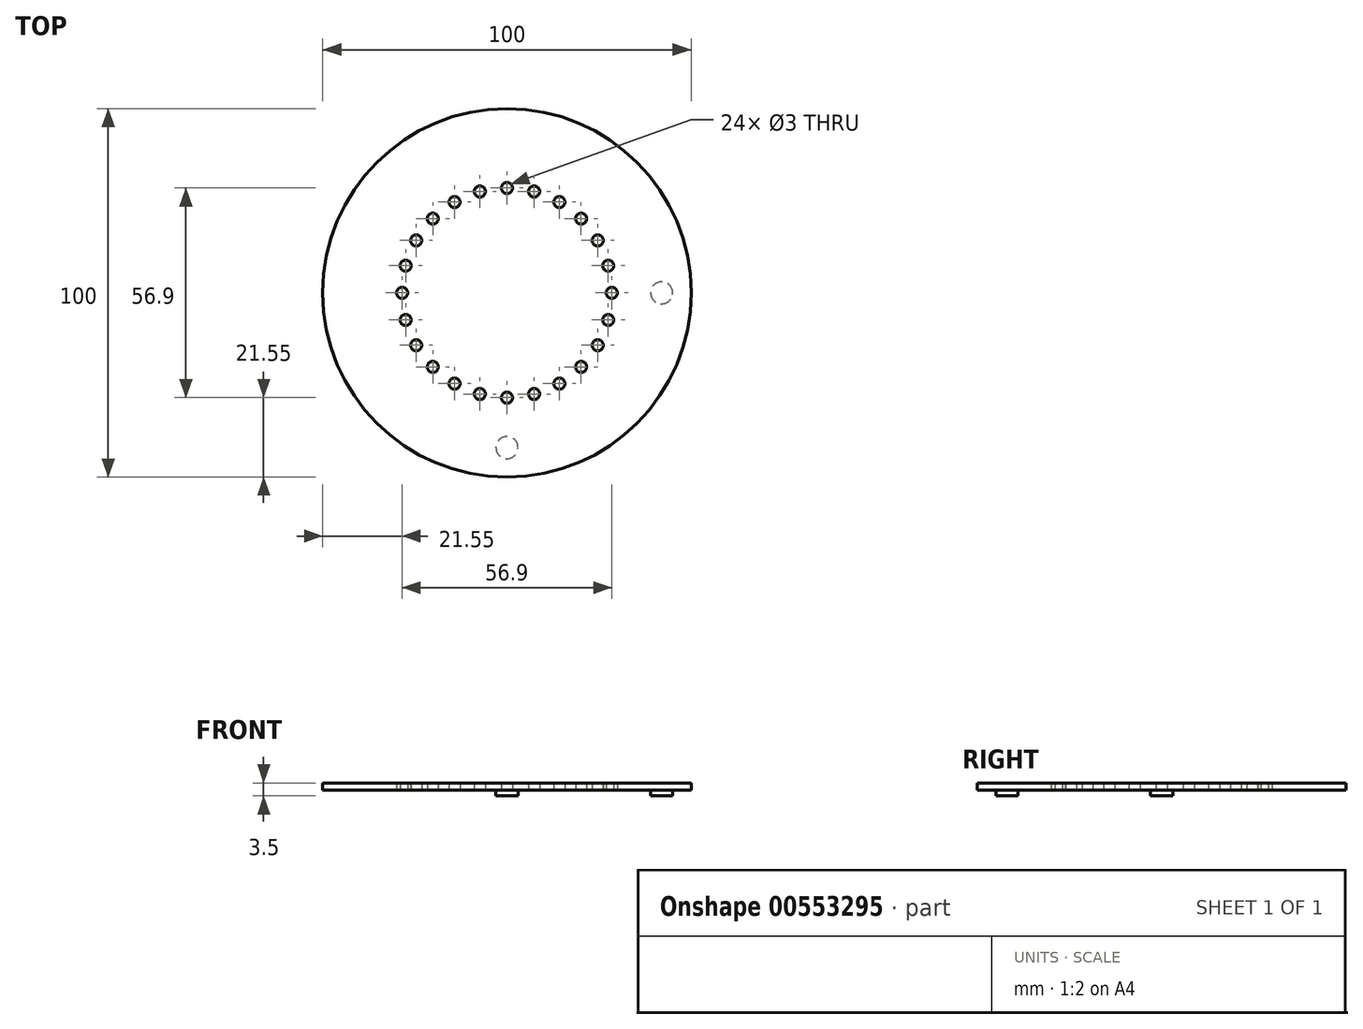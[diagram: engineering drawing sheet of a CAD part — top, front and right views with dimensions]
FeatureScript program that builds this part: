
annotation { "Feature Type Name" : "Feature", "Feature Type Description" : "" }
export const myFeature = defineFeature(function(context is Context, id is Id, definition is map)
    precondition{}
    {
        {
            var Q0;
            Q0=qCreatedBy(makeId("Top.planeOp"),FACE);
            var sketch = newSketch(context, id + "F0", { "sketchPlane" : qUnion([Q0])});
            skCircle(sketch, "E0", {"center": v(0, 0) * mm, "radius": 50 * mm});
            skCircle(sketch, "E1", {"center": v(0, 28.45) * mm, "radius": 1.5 * mm});
            skCircle(sketch, "E2.1.0", {"center": v(-7.36, 27.48) * mm, "radius": 1.5 * mm});
            skCircle(sketch, "E2.2.0", {"center": v(-14.22, 24.64) * mm, "radius": 1.5 * mm});
            skCircle(sketch, "E3.1.3.0", {"center": v(-20.12, 20.12) * mm, "radius": 1.5 * mm});
            skCircle(sketch, "E3.1.4.0", {"center": v(-24.64, 14.23) * mm, "radius": 1.5 * mm});
            skCircle(sketch, "E3.1.5.0", {"center": v(-27.48, 7.36) * mm, "radius": 1.5 * mm});
            skCircle(sketch, "E3.1.6.0", {"center": v(-28.45, 0) * mm, "radius": 1.5 * mm});
            skCircle(sketch, "E3.1.7.0", {"center": v(-27.48, -7.36) * mm, "radius": 1.5 * mm});
            skCircle(sketch, "E3.1.8.0", {"center": v(-24.64, -14.22) * mm, "radius": 1.5 * mm});
            skCircle(sketch, "E3.1.9.0", {"center": v(-20.12, -20.12) * mm, "radius": 1.5 * mm});
            skCircle(sketch, "E3.1.10.0", {"center": v(-14.22, -24.64) * mm, "radius": 1.5 * mm});
            skCircle(sketch, "E3.1.11.0", {"center": v(-7.36, -27.48) * mm, "radius": 1.5 * mm});
            skCircle(sketch, "E3.1.12.0", {"center": v(0, -28.45) * mm, "radius": 1.5 * mm});
            skCircle(sketch, "E3.1.13.0", {"center": v(7.36, -27.48) * mm, "radius": 1.5 * mm});
            skCircle(sketch, "E3.1.14.0", {"center": v(14.22, -24.64) * mm, "radius": 1.5 * mm});
            skCircle(sketch, "E3.1.15.0", {"center": v(20.12, -20.12) * mm, "radius": 1.5 * mm});
            skCircle(sketch, "E3.1.16.0", {"center": v(24.64, -14.23) * mm, "radius": 1.5 * mm});
            skCircle(sketch, "E3.1.17.0", {"center": v(27.48, -7.36) * mm, "radius": 1.5 * mm});
            skCircle(sketch, "E3.1.18.0", {"center": v(28.45, 0) * mm, "radius": 1.5 * mm});
            skCircle(sketch, "E3.1.19.0", {"center": v(27.48, 7.36) * mm, "radius": 1.5 * mm});
            skCircle(sketch, "E3.1.20.0", {"center": v(24.64, 14.23) * mm, "radius": 1.5 * mm});
            skCircle(sketch, "E3.1.21.0", {"center": v(20.12, 20.12) * mm, "radius": 1.5 * mm});
            skCircle(sketch, "E3.1.22.0", {"center": v(14.23, 24.64) * mm, "radius": 1.5 * mm});
            skCircle(sketch, "E3.1.23.0", {"center": v(7.36, 27.48) * mm, "radius": 1.5 * mm});
            skSolve(sketch);
        }
        {
            var Q0;
            Q0=makeQuery(id+"F0.imprint","IMPRINT",FACE,{"disambiguationData":[TD([[makeQuery(id+"F0.imprint","IMPRINT",EDGE,{"derivedFrom":sQuery(id+"F0.wireOp",EDGE,"E0")}),1.0]])]});
            extrude(context, id + "F1", {"entities" : qUnion([Q0]), "depth" : 2 * mm, "offsetDistance" : 25 * mm});
        }
        {
            var Q0;
            Q0=makeQuery(id+"F1.opExtrude","CAP_FACE",FACE,{"disambiguationData":[OSD([sQuery(id+"F0.wireOp",EDGE,"E0"),sQuery(id+"F0.wireOp",EDGE,"E1"),sQuery(id+"F0.wireOp",EDGE,"E2.1.0"),sQuery(id+"F0.wireOp",EDGE,"E2.2.0"),sQuery(id+"F0.wireOp",EDGE,"E3.1.3.0"),sQuery(id+"F0.wireOp",EDGE,"E3.1.4.0"),sQuery(id+"F0.wireOp",EDGE,"E3.1.5.0"),sQuery(id+"F0.wireOp",EDGE,"E3.1.6.0"),sQuery(id+"F0.wireOp",EDGE,"E3.1.7.0"),sQuery(id+"F0.wireOp",EDGE,"E3.1.8.0"),sQuery(id+"F0.wireOp",EDGE,"E3.1.9.0"),sQuery(id+"F0.wireOp",EDGE,"E3.1.10.0"),sQuery(id+"F0.wireOp",EDGE,"E3.1.11.0"),sQuery(id+"F0.wireOp",EDGE,"E3.1.12.0"),sQuery(id+"F0.wireOp",EDGE,"E3.1.13.0"),sQuery(id+"F0.wireOp",EDGE,"E3.1.14.0"),sQuery(id+"F0.wireOp",EDGE,"E3.1.15.0"),sQuery(id+"F0.wireOp",EDGE,"E3.1.16.0"),sQuery(id+"F0.wireOp",EDGE,"E3.1.17.0"),sQuery(id+"F0.wireOp",EDGE,"E3.1.18.0"),sQuery(id+"F0.wireOp",EDGE,"E3.1.19.0"),sQuery(id+"F0.wireOp",EDGE,"E3.1.20.0"),sQuery(id+"F0.wireOp",EDGE,"E3.1.21.0"),sQuery(id+"F0.wireOp",EDGE,"E3.1.22.0"),sQuery(id+"F0.wireOp",EDGE,"E3.1.23.0")])],"isStart":true});
            var sketch = newSketch(context, id + "F2", { "sketchPlane" : qUnion([Q0])});
            skCircle(sketch, "E4", {"center": v(0, 42) * mm, "radius": 3 * mm});
            skCircle(sketch, "E5", {"center": v(42, 0) * mm, "radius": 3 * mm});
            skSolve(sketch);
        }
        {
            var Q0;
            Q0=makeQuery(id+"F2.imprint","IMPRINT",FACE,{"disambiguationData":[TD([[makeQuery(id+"F2.imprint","IMPRINT",EDGE,{"derivedFrom":sQuery(id+"F2.wireOp",EDGE,"E4")}),1.0]])]});
            var Q1;
            Q1=makeQuery(id+"F2.imprint","IMPRINT",FACE,{"disambiguationData":[TD([[makeQuery(id+"F2.imprint","IMPRINT",EDGE,{"derivedFrom":sQuery(id+"F2.wireOp",EDGE,"E5")}),1.0]])]});
            extrude(context, id + "F3", {"entities" : qUnion([Q0, Q1]), "operationType" : NewBodyOperationType.ADD, "depth" : 1.5 * mm, "offsetDistance" : 25 * mm});
        }
    });
